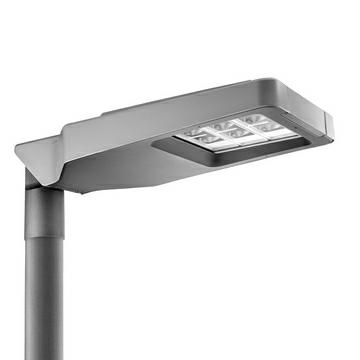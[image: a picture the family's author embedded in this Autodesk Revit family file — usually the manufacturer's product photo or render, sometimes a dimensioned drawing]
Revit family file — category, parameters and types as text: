
# Revit family: Lighting-StreetLighting-GEWISS-ROAD[5]MINI-LED_OPTIC_HUGE_CLI
name_source: partatom
category: Apparecchi per illuminazione
units: mm (PartAtom-declared; Revit-internal decimal feet)

## family parameters
Basato su piano di lavoro = No
Condiviso = No
Punto di calcolo locali = No
Quota connettore circolare = Usa diametro
Sempre verticale = Sì
Sorgente d'illuminazione = No
Taglio con vuoti quando caricato = No
Tipo di parte = Normale

## types (26) — shared parameters
Applicazione = External
Carico apparente = 53 VA
Catalogue = LIGHTING
Catalogue Range = ROAD [5]
Commenti sul wattaggio = 53W
Electrocod = 244C
IDF = 0fc73019-b15a-4bb7-a903-3c2ad933a49c
IDT = 6eb1c969380f487eb4332d009c9c34aa
IP degree = IP66
Immagine tipo = GWR5276M.jpg
Insulation class = I
Lamp- = LED
Lampada = LED
Minimum distance from the illuminated object = 1M
Produttore = GEWISS S.p.A.
SEO = Street lighting
Shock resistance = IK08
Technical sheet = https://www.gewiss.com
Tilt adjustable = -20° ÷ +10° side bracket - -10° ÷ +20° pole head
Tipo alimentatore = Constant Current Driver Led
URL = https://www.gewiss.com
Version file RFA = 20.11
Warranty = 5 years

## per-type parameters (varying)
- GWR5611M - ROAD5 MINI HUGE 1M 4000K 1,0A CL1 1-10V: Colour temperature=4000 K (CRI 70); Colour temperature:=4000 K (CRI 70); Descrizione=ROAD5 MINI HUGE 1M 4000K 1,0A CL1 1-10V; EAN code=8011564874053; LED LifeTime (L80B05)=120000H; LED current.=1A; Lumen output (lm)=3370; Maximum surface exposed to the wind=0,15M2; Modello=GWR5611M; No. Chorus modules=1 (1x3 LED); Nominal flux (lm)=4770; Number of modules=1 (1x3 LED); Operating temperature:=-25 +40 °C; Optic=H - ULOR: 0%; Overvoltage resistance=12 KV (Common and dfferential mode); Pilot current=1A; Power supply operation=Dimmable; System power=38W; Tipologia=Dimmable; Voltage-=220/240 V - 50/60 Hz - Dimmable 1-10 V; Weight (kg)=6,4; Weight (kg):=6,4; Working temperature=-25 +40 °C
- GWR5612B30K - ROAD5 MINI HUGE 2M 3000K 1,0A CL1 BIREG: Body=Die-cast aluminium -; Classification:=-; Color Rendering Index=CRI-70; Colore=Graphite grey; Colour :=Powder coating; Colour temperature=3000K; Colour temperature:=3000 K (CRI>80); Context=Street and parking lighting; Control System=Bi-power with self-learning; DIN 18032-3 certification=-; Descrizione=GWR5612B30K - ROAD5 MINI HUGE 2M 3000K 1,0A CL1 BIREG; Device with reduced surface temperature=-; Driver=Included; Driver Box=Built-in; Efficiency (lm/W)=91; Eletrical and lighting features=-; External screw=Stainless steel; Fixing=Pole Head - Outreach; Gasket=Anti-aging silicone; General information=-; Glow Wire Test :=-; IPEA=ROAD = A + // LARGE AREAS = A + // CYCLOPEDONALS = A // GREEN AREAS = A // HISTORICAL CENTER = A4 +; Installationa and maintenance=-; LED Life Time (L80B05)=120000H; LED Maintenance=Not available; LED current.=1A; Lifetime=L90B10 (Tq+25°C) = 100.000 h - L90B10 (Tq+40°C) = 75.000 h; Locking Hook=Integrated front handle; Lumen output (lm)=7000; Luminaire=LED Road Equipment; Materials=-; Maximum surface exposed to the wind=0,149999999999999M2; Maximum surface exposed to the wind :=0.15 m²; Modello=GWR5612B30K; Mouting and installation=Pole Head - Outreach; Nominal flux (lm)=8280; Number of modules=2 (2x3 LED); Operating temperature :=-25 +40 °C; Operating temperature:=-25 +40 °C; Optic=HUGE; Optic :=Metallized polycarbonate reflector; Optic Maintenance=Not available; Optic and illuminating features=-; Overvoltage protection=DM 10KV / CM 10KV; Overvoltage resistance :=Common and dfferential mode: 10KV; Photobiological Risk Class=RG0; Power supply operation=Bi power; Rated frequency (Hz)=50 / 60; Shield type=4mm thick flat tempered glass; Standard Deviation Colour Matching=SDCM = 5; Standard-=EN 60598-2-3, EN 60598-1 IEC/TR 62778; Standards and approvals=-; Stocking temperature=-; Supply voltage=220 - 240 V; System power=77W; System power :=77 W @ 1A; Tilt-=-20° ÷ +10° side bracket - -10° ÷ +20° pole head; Tipologia=Bi power; Type of light source=LED - Not replaceable; Unified Glare Rating=G*3 - ULOR = 0; Unique digital code (Datamatrix)=Currently not present; Voltage-=220/240 V - 50/60 Hz - Bi-power with self-learning; Weight (kg):=6,6; Wiring=Isolating switch
- GWR561130K - ROAD5 MINI HUGE 1M 3000K 1,0A CL1: Body=Die-cast aluminium -; Classification:=-; Color Rendering Index=CRI-70; Colore=Graphite grey; Colour :=Powder coating; Colour temperature=3000K; Colour temperature:=3000 K (CRI>80); Context=Street and parking lighting; Control System=Stand alone; DIN 18032-3 certification=-; Descrizione=GWR561130K - ROAD5 MINI HUGE 1M 3000K 1,0A CL1; Device with reduced surface temperature=-; Driver=Included; Driver Box=Built-in; Efficiency (lm/W)=92; Eletrical and lighting features=-; External screw=Stainless steel; Fixing=Pole Head - Outreach; Gasket=Anti-aging silicone; General information=-; Glow Wire Test :=-; IPEA=ROAD = A + // LARGE AREAS = A ++ // CYCLOPEDONALS = A + // GREEN AREAS = A + // HISTORICAL CENTER = A4 +; Installationa and maintenance=-; LED Life Time (L80B05)=120000H; LED Maintenance=Not available; LED current.=1A; Lifetime=L90B10 (Tq+25°C) = 100.000 h - L90B10 (Tq+40°C) = 75.000 h; Locking Hook=Integrated front handle; Lumen output (lm)=3500; Luminaire=LED Road Equipment; Materials=-; Maximum surface exposed to the wind=0,149999999999999M2; Maximum surface exposed to the wind :=0.15 m²; Modello=GWR561130K; Mouting and installation=Pole Head - Outreach; Nominal flux (lm)=4140; Number of modules=1 (1x3 LED); Operating temperature :=-25 +40 °C; Operating temperature:=-25 +40 °C; Optic=HUGE; Optic :=Metallized polycarbonate reflector; Optic Maintenance=Not available; Optic and illuminating features=-; Overvoltage protection=DM 10KV / CM 10KV; Overvoltage resistance :=Common and dfferential mode: 10KV; Photobiological Risk Class=RG0; Rated frequency (Hz)=50 / 60; Shield type=4mm thick flat tempered glass; Standard Deviation Colour Matching=SDCM = 5; Standard-=EN 60598-2-3, EN 60598-1 IEC/TR 62778; Standards and approvals=-; Stocking temperature=-; Supply voltage=220 - 240 V; System power=38W; System power :=38 W @ 1A; Tilt-=-20° ÷ +10° side bracket - -10° ÷ +20° pole head; Tipologia=Stand alone; Type of light source=LED - Not replaceable; Unified Glare Rating=G*3 - ULOR = 0; Unique digital code (Datamatrix)=Currently not present; Voltage-=220/240 V - 50/60 Hz - Stand alone; Weight (kg):=6,4; Wiring=Isolating switch
- GWR5672M - ROAD5 MINI HUGE 2M 4000K 0,7A CL1 1-10V: Colour temperature=4000 K (CRI 70); Colour temperature:=4000 K (CRI 70); Descrizione=ROAD5 MINI HUGE 2M 4000K 0,7A CL1 1-10V; EAN code=8011564874473; LED LifeTime (L80B05)=77000H; LED current.=0,7A; Lumen output (lm)=4590; Maximum surface exposed to the wind=0,15M2; Modello=GWR5672M; No. Chorus modules=2 (2x3 LED); Nominal flux (lm)=6240; Number of modules=2 (2x3 LED); Operating temperature:=-25 +50 °C; Optic=H - ULOR: 0%; Overvoltage resistance=12 KV (Common and dfferential mode); Pilot current=0,7A; Power supply operation=Dimmable; System power=53W; Tipologia=Dimmable; Voltage-=220/240 V - 50/60 Hz - Dimmable 1-10 V; Weight (kg)=6,6; Weight (kg):=6,6; Working temperature=-25 +50 °C
- GWR5611B30K - ROAD5 MINI HUGE 1M 3000K 1,0A CL1 BIREG: Body=Die-cast aluminium -; Classification:=-; Color Rendering Index=CRI-70; Colore=Graphite grey; Colour :=Powder coating; Colour temperature=3000K; Colour temperature:=3000 K (CRI>80); Context=Street and parking lighting; Control System=Bi-power with self-learning; DIN 18032-3 certification=-; Descrizione=GWR5611B30K - ROAD5 MINI HUGE 1M 3000K 1,0A CL1 BIREG; Device with reduced surface temperature=-; Driver=Included; Driver Box=Built-in; Efficiency (lm/W)=90; Eletrical and lighting features=-; External screw=Stainless steel; Fixing=Pole Head - Outreach; Gasket=Anti-aging silicone; General information=-; Glow Wire Test :=-; IPEA=ROAD = A + // LARGE AREAS = A + // CYCLOPEDONALS = A // GREEN AREAS = A // HISTORICAL CENTER = A3 +; Installationa and maintenance=-; LED Life Time (L80B05)=120000H; LED Maintenance=Not available; LED current.=1A; Lifetime=L90B10 (Tq+25°C) = 100.000 h - L90B10 (Tq+40°C) = 75.000 h; Locking Hook=Integrated front handle; Lumen output (lm)=3500; Luminaire=LED Road Equipment; Materials=-; Maximum surface exposed to the wind=0,149999999999999M2; Maximum surface exposed to the wind :=0.15 m²; Modello=GWR5611B30K; Mouting and installation=Pole Head - Outreach; Nominal flux (lm)=4140; Number of modules=1 (1x3 LED); Operating temperature :=-25 +40 °C; Operating temperature:=-25 +40 °C; Optic=HUGE; Optic :=Metallized polycarbonate reflector; Optic Maintenance=Not available; Optic and illuminating features=-; Overvoltage protection=DM 10KV / CM 10KV; Overvoltage resistance :=Common and dfferential mode: 10KV; Photobiological Risk Class=RG0; Power supply operation=Bi power; Rated frequency (Hz)=50 / 60; Shield type=4mm thick flat tempered glass; Standard Deviation Colour Matching=SDCM = 5; Standard-=EN 60598-2-3, EN 60598-1 IEC/TR 62778; Standards and approvals=-; Stocking temperature=-; Supply voltage=220 - 240 V; System power=39W; System power :=39 W @ 1A; Tilt-=-20° ÷ +10° side bracket - -10° ÷ +20° pole head; Tipologia=Bi power; Type of light source=LED - Not replaceable; Unified Glare Rating=G*3 - ULOR = 0; Unique digital code (Datamatrix)=Currently not present; Voltage-=220/240 V - 50/60 Hz - Bi-power with self-learning; Weight (kg):=6,4; Wiring=Isolating switch
- GWR5612M - ROAD5 MINI HUGE 2M 4000K 1,0A CL1 1-10V: Colour temperature=4000 K (CRI 70); Colour temperature:=4000 K (CRI 70); Descrizione=ROAD5 MINI HUGE 2M 4000K 1,0A CL1 1-10V; EAN code=8011564874084; LED LifeTime (L80B05)=120000H; LED current.=1A; Lumen output (lm)=6730; Maximum surface exposed to the wind=0,15M2; Modello=GWR5612M; No. Chorus modules=2 (2x3 LED); Nominal flux (lm)=9540; Number of modules=2 (2x3 LED); Operating temperature:=-25 +40 °C; Optic=H - ULOR: 0%; Overvoltage resistance=12 KV (Common and dfferential mode); Pilot current=1A; Power supply operation=Dimmable; System power=76W; Tipologia=Dimmable; Voltage-=220/240 V - 50/60 Hz - Dimmable 1-10 V; Weight (kg)=6,6; Weight (kg):=6,6; Working temperature=-25 +40 °C
- GWR5671M - ROAD5 MINI HUGE 1M 4000K 0,7A CL1 1-10V: Colour temperature=4000 K (CRI 70); Colour temperature:=4000 K (CRI 70); Descrizione=ROAD5 MINI HUGE 1M 4000K 0,7A CL1 1-10V; EAN code=8011564874442; LED LifeTime (L80B05)=77000H; LED current.=0,7A; Lumen output (lm)=2300; Maximum surface exposed to the wind=0,15M2; Modello=GWR5671M; No. Chorus modules=1 (1x3 LED); Nominal flux (lm)=3120; Number of modules=1 (1x3 LED); Operating temperature:=-25 +50 °C; Optic=H - ULOR: 0%; Overvoltage resistance=12 KV (Common and dfferential mode); Pilot current=0,7A; Power supply operation=Dimmable; System power=27W; Tipologia=Dimmable; Voltage-=220/240 V - 50/60 Hz - Dimmable 1-10 V; Weight (kg)=6,4; Weight (kg):=6,4; Working temperature=-25 +50 °C
- GWR5612 - ROAD5 MINI HUGE 2M 4000K 1,0A CL1: Colour temperature=4000 K (CRI 70); Colour temperature:=4000 K (CRI 70); Descrizione=ROAD5 MINI HUGE 2M 4000K 1,0A CL1; EAN code=8011564874060; LED LifeTime (L80B05)=120000H; LED current.=1A; Lumen output (lm)=6730; Maximum surface exposed to the wind=0,15M2; Modello=GWR5612; No. Chorus modules=2 (2x3 LED); Nominal flux (lm)=9540; Number of modules=2 (2x3 LED); Operating temperature:=-25 +40 °C; Optic=H - ULOR: 0%; Overvoltage resistance=12 KV (Common and dfferential mode); Pilot current=1A; System power=76W; Tipologia=Stand alone; Voltage-=220/240 V - 50/60 Hz - Stand alone; Weight (kg)=6,6; Weight (kg):=6,6; Working temperature=-25 +40 °C
- GWR5612B - ROAD5 MINI HUGE 2M 4000K 1,0A CL1 BIREG: Colour temperature=4000 K (CRI 70); Colour temperature:=4000 K (CRI 70); Descrizione=ROAD5 MINI HUGE 2M 4000K 1,0A CL1 BI-POW; EAN code=8011564874077; LED LifeTime (L80B05)=120000H; LED current.=1A; Lumen output (lm)=6730; Maximum surface exposed to the wind=0,15M2; Modello=GWR5612B; No. Chorus modules=2 (2x3 LED); Nominal flux (lm)=9540; Number of modules=2 (2x3 LED); Operating temperature:=-25 +40 °C; Optic=H - ULOR: 0%; Overvoltage resistance=12 KV (Common and dfferential mode); Pilot current=1A; Power supply operation=Bi power; System power=77W; Tipologia=Bi power; Voltage-=220/240 V - 50/60 Hz - Bi-power with self-learning; Weight (kg)=6,6; Weight (kg):=6,6; Working temperature=-25 +40 °C
- GWR5671 - ROAD5 MINI HUGE 1M 4000K 0,7A CL1: Colour temperature=4000 K (CRI 70); Colour temperature:=4000 K (CRI 70); Descrizione=ROAD5 MINI HUGE 1M 4000K 0,7A CL1; EAN code=8011564874428; LED LifeTime (L80B05)=77000H; LED current.=0,7A; Lumen output (lm)=2300; Maximum surface exposed to the wind=0,15M2; Modello=GWR5671; No. Chorus modules=1 (1x3 LED); Nominal flux (lm)=3120; Number of modules=1 (1x3 LED); Operating temperature:=-25 +50 °C; Optic=H - ULOR: 0%; Overvoltage resistance=12 KV (Common and dfferential mode); Pilot current=0,7A; System power=27W; Tipologia=Stand alone; Voltage-=220/240 V - 50/60 Hz - Stand alone; Weight (kg)=6,4; Weight (kg):=6,4; Working temperature=-25 +50 °C
- GWR5611M30K - ROAD5 MINI HUGE 1M 3000K 1,0A CL1 1-10V: Body=Die-cast aluminium -; Classification:=-; Color Rendering Index=CRI-70; Colore=Graphite grey; Colour :=Powder coating; Colour temperature=3000K; Colour temperature:=3000 K (CRI>80); Context=Street and parking lighting; Control System=Dimmable 1-10 V; DIN 18032-3 certification=-; Descrizione=GWR5611M30K - ROAD5 MINI HUGE 1M 3000K 1,0A CL1 1-10V; Device with reduced surface temperature=-; Driver=Included; Driver Box=Built-in; Efficiency (lm/W)=90; Eletrical and lighting features=-; External screw=Stainless steel; Fixing=Pole Head - Outreach; Gasket=Anti-aging silicone; General information=-; Glow Wire Test :=-; IPEA=ROAD = A + // LARGE AREAS = A + // CYCLOPEDONALS = A // GREEN AREAS = A // HISTORICAL CENTER = A3 +; Installationa and maintenance=-; LED Life Time (L80B05)=120000H; LED Maintenance=Not available; LED current.=1A; Lifetime=L90B10 (Tq+25°C) = 100.000 h - L90B10 (Tq+40°C) = 75.000 h; Locking Hook=Integrated front handle; Lumen output (lm)=3500; Luminaire=LED Road Equipment; Materials=-; Maximum surface exposed to the wind=0,149999999999999M2; Maximum surface exposed to the wind :=0.15 m²; Modello=GWR5611M30K; Mouting and installation=Pole Head - Outreach; Nominal flux (lm)=4140; Number of modules=1 (1x3 LED); Operating temperature :=-25 +40 °C; Operating temperature:=-25 +40 °C; Optic=HUGE; Optic :=Metallized polycarbonate reflector; Optic Maintenance=Not available; Optic and illuminating features=-; Overvoltage protection=DM 10KV / CM 10KV; Overvoltage resistance :=Common and dfferential mode: 10KV; Photobiological Risk Class=RG0; Power supply operation=Dimmable; Rated frequency (Hz)=50 / 60; Shield type=4mm thick flat tempered glass; Standard Deviation Colour Matching=SDCM = 5; Standard-=EN 60598-2-3, EN 60598-1 IEC/TR 62778; Standards and approvals=-; Stocking temperature=-; Supply voltage=220 - 240 V; System power=38W; System power :=39 W @ 1A; Tilt-=-20° ÷ +10° side bracket - -10° ÷ +20° pole head; Tipologia=Dimmable; Type of light source=LED - Not replaceable; Unified Glare Rating=G*3 - ULOR = 0; Unique digital code (Datamatrix)=Currently not present; Voltage-=220/240 V - 50/60 Hz - Dimmable 1-10 V; Weight (kg):=6,4; Wiring=Isolating switch
- GWR5672M30K - ROAD5 MINI HUGE 2M 3000K 0,7A CL1 1-10V: Body=Die-cast aluminium -; Classification:=-; Color Rendering Index=CRI-70; Colore=Graphite grey; Colour :=Powder coating; Colour temperature=3000K; Colour temperature:=3000 K (CRI>80); Context=Street and parking lighting; Control System=Dimmable 1-10 V; DIN 18032-3 certification=-; Descrizione=GWR5672M30K - ROAD5 MINI HUGE 2M 3000K 0,7A CL1 1-10V; Device with reduced surface temperature=-; Driver=Included; Driver Box=Built-in; Efficiency (lm/W)=96; Eletrical and lighting features=-; External screw=Stainless steel; Fixing=Pole Head - Outreach; Gasket=Anti-aging silicone; General information=-; Glow Wire Test :=-; IPEA=ROAD = A ++ // LARGE AREAS = A ++ // CYCLOPEDONALS = A + // GREEN AREAS = A + // HISTORICAL CENTER = A5 +; Installationa and maintenance=-; LED Life Time (L80B05)=77000H; LED Maintenance=Not available; LED current.=0,7A; Lifetime=L90B10 (Tq+25°C) = 100.000 h - L90B10 (Tq+50°C) = 75.000 h; Locking Hook=Integrated front handle; Lumen output (lm)=5200; Luminaire=LED Road Equipment; Materials=-; Maximum surface exposed to the wind=0,149999999999999M2; Maximum surface exposed to the wind :=0.15 m²; Modello=GWR5672M30K; Mouting and installation=Pole Head - Outreach; Nominal flux (lm)=5400; Number of modules=2 (2x3 LED); Operating temperature :=-25 +50 °C; Operating temperature:=-25 +50 °C; Optic=HUGE; Optic :=Metallized polycarbonate reflector; Optic Maintenance=Not available; Optic and illuminating features=-; Overvoltage protection=DM 10KV / CM 10KV; Overvoltage resistance :=Common and dfferential mode: 10KV; Photobiological Risk Class=RG0; Power supply operation=Dimmable; Rated frequency (Hz)=50 / 60; Shield type=4mm thick flat tempered glass; Standard Deviation Colour Matching=SDCM = 5; Standard-=EN 60598-2-3, EN 60598-1 IEC/TR 62778; Standards and approvals=-; Stocking temperature=-; Supply voltage=220 - 240 V; System power=53W; System power :=54 W @ 0.7A; Tilt-=-20° ÷ +10° side bracket - -10° ÷ +20° pole head; Tipologia=Dimmable; Type of light source=LED - Not replaceable; Unified Glare Rating=G*3 - ULOR = 0; Unique digital code (Datamatrix)=Currently not present; Voltage-=220/240 V - 50/60 Hz - Dimmable 1-10 V; Weight (kg):=6,6; Wiring=Isolating switch
- GWR561230K - ROAD5 MINI HUGE 2M 3000K 1,0A CL1: Body=Die-cast aluminium -; Classification:=-; Color Rendering Index=CRI-70; Colore=Graphite grey; Colour :=Powder coating; Colour temperature=3000K; Colour temperature:=3000 K (CRI>80); Context=Street and parking lighting; Control System=Stand alone; DIN 18032-3 certification=-; Descrizione=GWR561230K - ROAD5 MINI HUGE 2M 3000K 1,0A CL1; Device with reduced surface temperature=-; Driver=Included; Driver Box=Built-in; Efficiency (lm/W)=97; Eletrical and lighting features=-; External screw=Stainless steel; Fixing=Pole Head - Outreach; Gasket=Anti-aging silicone; General information=-; Glow Wire Test :=-; IPEA=ROAD = A + // LARGE AREAS = A ++ // CYCLOPEDONALS = A + // GREEN AREAS = A + // HISTORICAL CENTER = A5 +; Installationa and maintenance=-; LED Life Time (L80B05)=120000H; LED Maintenance=Not available; LED current.=0,9A; Lifetime=L90B10 (Tq+25°C) = 100.000 h - L90B10 (Tq+40°C) = 75.000 h; Locking Hook=Integrated front handle; Lumen output (lm)=6500; Luminaire=LED Road Equipment; Materials=-; Maximum surface exposed to the wind=0,149999999999999M2; Maximum surface exposed to the wind :=0.15 m²; Modello=GWR561230K; Mouting and installation=Pole Head - Outreach; Nominal flux (lm)=8280; Number of modules=2 (2x3 LED); Operating temperature :=-25 +40 °C; Operating temperature:=-25 +40 °C; Optic=HUGE; Optic :=Metallized polycarbonate reflector; Optic Maintenance=Not available; Optic and illuminating features=-; Overvoltage protection=DM 10KV / CM 10KV; Overvoltage resistance :=Common and dfferential mode: 10KV; Photobiological Risk Class=RG0; Rated frequency (Hz)=50 / 60; Shield type=4mm thick flat tempered glass; Standard Deviation Colour Matching=SDCM = 5; Standard-=EN 60598-2-3, EN 60598-1 IEC/TR 62778; Standards and approvals=-; Stocking temperature=-; Supply voltage=220 - 240 V; System power=76W; System power :=67 W @ 0.9A; Tilt-=-20° ÷ +10° side bracket - -10° ÷ +20° pole head; Tipologia=Stand alone; Type of light source=LED - Not replaceable; Unified Glare Rating=G*3 - ULOR = 0; Unique digital code (Datamatrix)=Currently not present; Voltage-=220/240 V - 50/60 Hz - Stand alone; Weight (kg):=6,6; Wiring=Isolating switch
- GWR5631 - ROAD5 MINI HUGE 1M 4000K 0,35A CL1: Colour temperature=4000 K (CRI 70); Colour temperature:=4000 K (CRI 70); Descrizione=ROAD5 MINI HUGE 1M 4000K 0,35A CL1; EAN code=8011564874411; LED LifeTime (L80B05)=77000H; LED current.=0,35A; Lumen output (lm)=1150; Maximum surface exposed to the wind=0,15M2; Modello=GWR5631; No. Chorus modules=1 (1x3 LED); Nominal flux (lm)=1560; Number of modules=1 (1x3 LED); Operating temperature:=-25 +50 °C; Optic=H - ULOR: 0%; Overvoltage resistance=12 KV (Common and dfferential mode); Pilot current=0,35A; System power=14W; Tipologia=Stand alone; Voltage-=220/240 V - 50/60 Hz - Stand alone; Weight (kg)=6,4; Weight (kg):=6,4; Working temperature=-25 +50 °C
- GWR5671B - ROAD5 MINI HUGE 1M 4000K 0,7A CL1 BIREG: Colour temperature=4000 K (CRI 70); Colour temperature:=4000 K (CRI 70); Descrizione=ROAD5 MINI HUGE 1M 4000K 0,7A CL1 BI-POW; EAN code=8011564874435; LED LifeTime (L80B05)=77000H; LED current.=0,7A; Lumen output (lm)=2300; Maximum surface exposed to the wind=0,15M2; Modello=GWR5671B; No. Chorus modules=1 (1x3 LED); Nominal flux (lm)=3120; Number of modules=1 (1x3 LED); Operating temperature:=-25 +50 °C; Optic=H - ULOR: 0%; Overvoltage resistance=12 KV (Common and dfferential mode); Pilot current=0,7A; Power supply operation=Bi power; System power=28W; Tipologia=Bi power; Voltage-=220/240 V - 50/60 Hz - Bi-power with self-learning; Weight (kg)=6,4; Weight (kg):=6,4; Working temperature=-25 +50 °C
- GWR5611B - ROAD5 MINI HUGE 1M 4000K 1,0A CL1 BIREG: Colour temperature=4000 K (CRI 70); Colour temperature:=4000 K (CRI 70); Descrizione=ROAD5 MINI HUGE 1M 4000K 1,0A CL1 BI-POW; EAN code=8011564874046; LED LifeTime (L80B05)=120000H; LED current.=1A; Lumen output (lm)=3370; Maximum surface exposed to the wind=0,15M2; Modello=GWR5611B; No. Chorus modules=1 (1x3 LED); Nominal flux (lm)=4770; Number of modules=1 (1x3 LED); Operating temperature:=-25 +40 °C; Optic=H - ULOR: 0%; Overvoltage resistance=12 KV (Common and dfferential mode); Pilot current=1A; Power supply operation=Bi power; System power=39W; Tipologia=Bi power; Voltage-=220/240 V - 50/60 Hz - Bi-power with self-learning; Weight (kg)=6,4; Weight (kg):=6,4; Working temperature=-25 +40 °C
- GWR5612M30K - ROAD5 MINI HUGE 2M 3000K 1,0A CL1 1-10V: Body=Die-cast aluminium -; Classification:=-; Color Rendering Index=CRI-70; Colore=Graphite grey; Colour :=Powder coating; Colour temperature=3000K; Colour temperature:=3000 K (CRI>80); Context=Street and parking lighting; Control System=Dimmable 1-10 V; DIN 18032-3 certification=-; Descrizione=GWR5612M30K - ROAD5 MINI HUGE 2M 3000K 1,0A CL1 1-10V; Device with reduced surface temperature=-; Driver=Included; Driver Box=Built-in; Efficiency (lm/W)=91; Eletrical and lighting features=-; External screw=Stainless steel; Fixing=Pole Head - Outreach; Gasket=Anti-aging silicone; General information=-; Glow Wire Test :=-; IPEA=ROAD = A + // LARGE AREAS = A + // CYCLOPEDONALS = A // GREEN AREAS = A // HISTORICAL CENTER = A4 +; Installationa and maintenance=-; LED Life Time (L80B05)=120000H; LED Maintenance=Not available; LED current.=1A; Lifetime=L90B10 (Tq+25°C) = 100.000 h - L90B10 (Tq+40°C) = 75.000 h; Locking Hook=Integrated front handle; Lumen output (lm)=7000; Luminaire=LED Road Equipment; Materials=-; Maximum surface exposed to the wind=0,149999999999999M2; Maximum surface exposed to the wind :=0.15 m²; Modello=GWR5612M30K; Mouting and installation=Pole Head - Outreach; Nominal flux (lm)=8280; Number of modules=2 (2x3 LED); Operating temperature :=-25 +40 °C; Operating temperature:=-25 +40 °C; Optic=HUGE; Optic :=Metallized polycarbonate reflector; Optic Maintenance=Not available; Optic and illuminating features=-; Overvoltage protection=DM 10KV / CM 10KV; Overvoltage resistance :=Common and dfferential mode: 10KV; Photobiological Risk Class=RG0; Power supply operation=Dimmable; Rated frequency (Hz)=50 / 60; Shield type=4mm thick flat tempered glass; Standard Deviation Colour Matching=SDCM = 5; Standard-=EN 60598-2-3, EN 60598-1 IEC/TR 62778; Standards and approvals=-; Stocking temperature=-; Supply voltage=220 - 240 V; System power=76W; System power :=77 W @ 1A; Tilt-=-20° ÷ +10° side bracket - -10° ÷ +20° pole head; Tipologia=Dimmable; Type of light source=LED - Not replaceable; Unified Glare Rating=G*3 - ULOR = 0; Unique digital code (Datamatrix)=Currently not present; Voltage-=220/240 V - 50/60 Hz - Dimmable 1-10 V; Weight (kg):=6,6; Wiring=Isolating switch
- GWR5671B30K - ROAD5 MINI HUGE 1M 3000K 0,7A CL1 BIREG: Body=Die-cast aluminium -; Classification:=-; Color Rendering Index=CRI-70; Colore=Graphite grey; Colour :=Powder coating; Colour temperature=3000K; Colour temperature:=3000 K (CRI>80); Context=Street and parking lighting; Control System=Bi-power with self-learning; DIN 18032-3 certification=-; Descrizione=GWR5671B30K - ROAD5 MINI HUGE 1M 3000K 0,7A CL1 BIREG; Device with reduced surface temperature=-; Driver=Included; Driver Box=Built-in; Efficiency (lm/W)=93; Eletrical and lighting features=-; External screw=Stainless steel; Fixing=Pole Head - Outreach; Gasket=Anti-aging silicone; General information=-; Glow Wire Test :=-; IPEA=ROAD = A + // LARGE AREAS = A ++ // CYCLOPEDONALS = A + // GREEN AREAS = A + // HISTORICAL CENTER = A4 +; Installationa and maintenance=-; LED Life Time (L80B05)=77000H; LED Maintenance=Not available; LED current.=0,7A; Lifetime=L90B10 (Tq+25°C) = 100.000 h - L90B10 (Tq+50°C) = 75.000 h; Locking Hook=Integrated front handle; Lumen output (lm)=2600; Luminaire=LED Road Equipment; Materials=-; Maximum surface exposed to the wind=0,149999999999999M2; Maximum surface exposed to the wind :=0.15 m²; Modello=GWR5671B30K; Mouting and installation=Pole Head - Outreach; Nominal flux (lm)=2700; Number of modules=1 (1x3 LED); Operating temperature :=-25 +50 °C; Operating temperature:=-25 +50 °C; Optic=HUGE; Optic :=Metallized polycarbonate reflector; Optic Maintenance=Not available; Optic and illuminating features=-; Overvoltage protection=DM 10KV / CM 10KV; Overvoltage resistance :=Common and dfferential mode: 10KV; Photobiological Risk Class=RG0; Power supply operation=Bi power; Rated frequency (Hz)=50 / 60; Shield type=4mm thick flat tempered glass; Standard Deviation Colour Matching=SDCM = 5; Standard-=EN 60598-2-3, EN 60598-1 IEC/TR 62778; Standards and approvals=-; Stocking temperature=-; Supply voltage=220 - 240 V; System power=28W; System power :=28 W @ 0.7A; Tilt-=-20° ÷ +10° side bracket - -10° ÷ +20° pole head; Tipologia=Bi power; Type of light source=LED - Not replaceable; Unified Glare Rating=G*3 - ULOR = 0; Unique digital code (Datamatrix)=Currently not present; Voltage-=220/240 V - 50/60 Hz - Bi-power with self-learning; Weight (kg):=6,4; Wiring=Isolating switch
- GWR5611 - ROAD5 MINI HUGE 1M 4000K 1,0A CL1: Colour temperature=4000 K (CRI 70); Colour temperature:=4000 K (CRI 70); Descrizione=ROAD5 MINI HUGE 1M 4000K 1,0A CL1; EAN code=8011564874039; LED LifeTime (L80B05)=120000H; LED current.=1A; Lumen output (lm)=3370; Maximum surface exposed to the wind=0,15M2; Modello=GWR5611; No. Chorus modules=1 (1x3 LED); Nominal flux (lm)=4770; Number of modules=1 (1x3 LED); Operating temperature:=-25 +40 °C; Optic=H - ULOR: 0%; Overvoltage resistance=12 KV (Common and dfferential mode); Pilot current=1A; System power=38W; Tipologia=Stand alone; Voltage-=220/240 V - 50/60 Hz - Stand alone; Weight (kg)=6,4; Weight (kg):=6,4; Working temperature=-25 +40 °C
- GWR567130K - ROAD5 MINI HUGE 1M 3000K 0,7A CL1: Body=Die-cast aluminium -; Classification:=-; Color Rendering Index=CRI-70; Colore=Graphite grey; Colour :=Powder coating; Colour temperature=3000K; Colour temperature:=3000 K (CRI>80); Context=Street and parking lighting; Control System=Stand alone; DIN 18032-3 certification=-; Descrizione=GWR567130K - ROAD5 MINI HUGE 1M 3000K 0,7A CL1; Device with reduced surface temperature=-; Driver=Included; Driver Box=Built-in; Efficiency (lm/W)=96; Eletrical and lighting features=-; External screw=Stainless steel; Fixing=Pole Head - Outreach; Gasket=Anti-aging silicone; General information=-; Glow Wire Test :=-; IPEA=ROAD = A ++ // LARGE AREAS = A ++ // CYCLOPEDONALS = A + // GREEN AREAS = A + // HISTORICAL CENTER = A5 +; Installationa and maintenance=-; LED Life Time (L80B05)=77000H; LED Maintenance=Not available; LED current.=0,7A; Lifetime=L90B10 (Tq+25°C) = 100.000 h - L90B10 (Tq+50°C) = 75.000 h; Locking Hook=Integrated front handle; Lumen output (lm)=2600; Luminaire=LED Road Equipment; Materials=-; Maximum surface exposed to the wind=0,149999999999999M2; Maximum surface exposed to the wind :=0.15 m²; Modello=GWR567130K; Mouting and installation=Pole Head - Outreach; Nominal flux (lm)=2700; Number of modules=1 (1x3 LED); Operating temperature :=-25 +50 °C; Operating temperature:=-25 +50 °C; Optic=HUGE; Optic :=Metallized polycarbonate reflector; Optic Maintenance=Not available; Optic and illuminating features=-; Overvoltage protection=DM 10KV / CM 10KV; Overvoltage resistance :=Common and dfferential mode: 10KV; Photobiological Risk Class=RG0; Rated frequency (Hz)=50 / 60; Shield type=4mm thick flat tempered glass; Standard Deviation Colour Matching=SDCM = 5; Standard-=EN 60598-2-3, EN 60598-1 IEC/TR 62778; Standards and approvals=-; Stocking temperature=-; Supply voltage=220 - 240 V; System power=27W; System power :=27 W @ 0.7A; Tilt-=-20° ÷ +10° side bracket - -10° ÷ +20° pole head; Tipologia=Stand alone; Type of light source=LED - Not replaceable; Unified Glare Rating=G*3 - ULOR = 0; Unique digital code (Datamatrix)=Currently not present; Voltage-=220/240 V - 50/60 Hz - Stand alone; Weight (kg):=6,4; Wiring=Isolating switch
- GWR563130K - ROAD5 MINI HUGE 1M 3000K 0,35A CL1: Body=Die-cast aluminium -; Classification:=-; Color Rendering Index=CRI-70; Colore=Graphite grey; Colour :=Powder coating; Colour temperature=3000K; Colour temperature:=3000 K (CRI>80); Context=Street and parking lighting; Control System=Stand alone; DIN 18032-3 certification=-; Descrizione=GWR563130K - ROAD5 MINI HUGE 1M 3000K 0,35A CL1; Device with reduced surface temperature=-; Driver=Included; Driver Box=Built-in; Efficiency (lm/W)=108; Eletrical and lighting features=-; External screw=Stainless steel; Fixing=Pole Head - Outreach; Gasket=Anti-aging silicone; General information=-; Glow Wire Test :=-; IPEA=ROAD = A3 + // LARGE AREAS = A4 + // CYCLOPEDONALS = A3 + // GREEN AREAS = A3 + // HISTORICAL CENTER = A6 +; Installationa and maintenance=-; LED Life Time (L80B05)=77000H; LED Maintenance=Not available; LED current.=0,35A; Lifetime=L90B10 (Tq+25°C) = 100.000 h - L90B10 (Tq+50°C) = 75.000 h; Locking Hook=Integrated front handle; Lumen output (lm)=1400; Luminaire=LED Road Equipment; Materials=-; Maximum surface exposed to the wind=0,149999999999999M2; Maximum surface exposed to the wind :=0.15 m²; Modello=GWR563130K; Mouting and installation=Pole Head - Outreach; Nominal flux (lm)=1350; Number of modules=1 (1x3 LED); Operating temperature :=-25 +50 °C; Operating temperature:=-25 +50 °C; Optic=HUGE; Optic :=Metallized polycarbonate reflector; Optic Maintenance=Not available; Optic and illuminating features=-; Overvoltage protection=DM 10KV / CM 10KV; Overvoltage resistance :=Common and dfferential mode: 10KV; Photobiological Risk Class=RG0; Rated frequency (Hz)=50 / 60; Shield type=4mm thick flat tempered glass; Standard Deviation Colour Matching=SDCM = 5; Standard-=EN 60598-2-3, EN 60598-1 IEC/TR 62778; Standards and approvals=-; Stocking temperature=-; Supply voltage=220 - 240 V; System power=14W; System power :=13 W @ 0.35A; Tilt-=-20° ÷ +10° side bracket - -10° ÷ +20° pole head; Tipologia=Stand alone; Type of light source=LED - Not replaceable; Unified Glare Rating=G*3 - ULOR = 0; Unique digital code (Datamatrix)=Currently not present; Voltage-=220/240 V - 50/60 Hz - Stand alone; Weight (kg):=6,4; Wiring=Isolating switch
- GWR5672B - ROAD5 MINI HUGE 2M 4000K 0,7A CL1 BIREG: Colour temperature=4000 K (CRI 70); Colour temperature:=4000 K (CRI 70); Descrizione=ROAD5 MINI HUGE 2M 4000K 0,7A CL1 BI-POW; EAN code=8011564874466; LED LifeTime (L80B05)=77000H; LED current.=0,7A; Lumen output (lm)=4590; Maximum surface exposed to the wind=0,15M2; Modello=GWR5672B; No. Chorus modules=2 (2x3 LED); Nominal flux (lm)=6240; Number of modules=2 (2x3 LED); Operating temperature:=-25 +50 °C; Optic=H - ULOR: 0%; Overvoltage resistance=12 KV (Common and dfferential mode); Pilot current=0,7A; Power supply operation=Bi power; System power=54W; Tipologia=Bi power; Voltage-=220/240 V - 50/60 Hz - Bi-power with self-learning; Weight (kg)=6,6; Weight (kg):=6,6; Working temperature=-25 +50 °C
- GWR5672B30K - ROAD5 MINI HUGE 2M 3000K 0,7A CL1 BIREG: Body=Die-cast aluminium -; Classification:=-; Color Rendering Index=CRI-70; Colore=Graphite grey; Colour :=Powder coating; Colour temperature=3000K; Colour temperature:=3000 K (CRI>80); Context=Street and parking lighting; Control System=Bi-power with self-learning; DIN 18032-3 certification=-; Descrizione=GWR5672B30K - ROAD5 MINI HUGE 2M 3000K 0,7A CL1 BIREG; Device with reduced surface temperature=-; Driver=Included; Driver Box=Built-in; Efficiency (lm/W)=96; Eletrical and lighting features=-; External screw=Stainless steel; Fixing=Pole Head - Outreach; Gasket=Anti-aging silicone; General information=-; Glow Wire Test :=-; IPEA=ROAD = A ++ // LARGE AREAS = A ++ // CYCLOPEDONALS = A + // GREEN AREAS = A + // HISTORICAL CENTER = A5 +; Installationa and maintenance=-; LED Life Time (L80B05)=77000H; LED Maintenance=Not available; LED current.=0,7A; Lifetime=L90B10 (Tq+25°C) = 100.000 h - L90B10 (Tq+50°C) = 75.000 h; Locking Hook=Integrated front handle; Lumen output (lm)=5200; Luminaire=LED Road Equipment; Materials=-; Maximum surface exposed to the wind=0,149999999999999M2; Maximum surface exposed to the wind :=0.15 m²; Modello=GWR5672B30K; Mouting and installation=Pole Head - Outreach; Nominal flux (lm)=5400; Number of modules=2 (2x3 LED); Operating temperature :=-25 +50 °C; Operating temperature:=-25 +50 °C; Optic=HUGE; Optic :=Metallized polycarbonate reflector; Optic Maintenance=Not available; Optic and illuminating features=-; Overvoltage protection=DM 10KV / CM 10KV; Overvoltage resistance :=Common and dfferential mode: 10KV; Photobiological Risk Class=RG0; Power supply operation=Bi power; Rated frequency (Hz)=50 / 60; Shield type=4mm thick flat tempered glass; Standard Deviation Colour Matching=SDCM = 5; Standard-=EN 60598-2-3, EN 60598-1 IEC/TR 62778; Standards and approvals=-; Stocking temperature=-; Supply voltage=220 - 240 V; System power=54W; System power :=54 W @ 0.7A; Tilt-=-20° ÷ +10° side bracket - -10° ÷ +20° pole head; Tipologia=Bi power; Type of light source=LED - Not replaceable; Unified Glare Rating=G*3 - ULOR = 0; Unique digital code (Datamatrix)=Currently not present; Voltage-=220/240 V - 50/60 Hz - Bi-power with self-learning; Weight (kg):=6,6; Wiring=Isolating switch
- GWR567230K - ROAD5 MINI HUGE 2M 3000K 0,7A CL1: Body=Die-cast aluminium -; Classification:=-; Color Rendering Index=CRI-70; Colore=Graphite grey; Colour :=Powder coating; Colour temperature=3000K; Colour temperature:=3000 K (CRI>80); Context=Street and parking lighting; Control System=Stand alone; DIN 18032-3 certification=-; Descrizione=GWR567230K - ROAD5 MINI HUGE 2M 3000K 0,7A CL1; Device with reduced surface temperature=-; Driver=Included; Driver Box=Built-in; Efficiency (lm/W)=98; Eletrical and lighting features=-; External screw=Stainless steel; Fixing=Pole Head - Outreach; Gasket=Anti-aging silicone; General information=-; Glow Wire Test :=-; IPEA=ROAD = A ++ // LARGE AREAS = A3 + // CYCLOPEDONALS = A ++ // GREEN AREAS = A ++ // HISTORICAL CENTER = A5 +; Installationa and maintenance=-; LED Life Time (L80B05)=77000H; LED Maintenance=Not available; LED current.=0,7A; Lifetime=L90B10 (Tq+25°C) = 100.000 h - L90B10 (Tq+50°C) = 75.000 h; Locking Hook=Integrated front handle; Lumen output (lm)=5200; Luminaire=LED Road Equipment; Materials=-; Maximum surface exposed to the wind=0,149999999999999M2; Maximum surface exposed to the wind :=0.15 m²; Modello=GWR567230K; Mouting and installation=Pole Head - Outreach; Nominal flux (lm)=5400; Number of modules=2 (2x3 LED); Operating temperature :=-25 +50 °C; Operating temperature:=-25 +50 °C; Optic=HUGE; Optic :=Metallized polycarbonate reflector; Optic Maintenance=Not available; Optic and illuminating features=-; Overvoltage protection=DM 10KV / CM 10KV; Overvoltage resistance :=Common and dfferential mode: 10KV; Photobiological Risk Class=RG0; Rated frequency (Hz)=50 / 60; Shield type=4mm thick flat tempered glass; Standard Deviation Colour Matching=SDCM = 5; Standard-=EN 60598-2-3, EN 60598-1 IEC/TR 62778; Standards and approvals=-; Stocking temperature=-; Supply voltage=220 - 240 V; System power=53W; System power :=53 W @ 0.7A; Tilt-=-20° ÷ +10° side bracket - -10° ÷ +20° pole head; Tipologia=Stand alone; Type of light source=LED - Not replaceable; Unified Glare Rating=G*3 - ULOR = 0; Unique digital code (Datamatrix)=Currently not present; Voltage-=220/240 V - 50/60 Hz - Stand alone; Weight (kg):=6,6; Wiring=Isolating switch
- GWR5672 - ROAD5 MINI HUGE 2M 4000K 0,7A CL1: Colour temperature=4000 K (CRI 70); Colour temperature:=4000 K (CRI 70); Descrizione=ROAD5 MINI HUGE 2M 4000K 0,7A CL1; EAN code=8011564874459; LED LifeTime (L80B05)=77000H; LED current.=0,7A; Lumen output (lm)=4590; Maximum surface exposed to the wind=0,15M2; Modello=GWR5672; No. Chorus modules=2 (2x3 LED); Nominal flux (lm)=6240; Number of modules=2 (2x3 LED); Operating temperature:=-25 +50 °C; Optic=H - ULOR: 0%; Overvoltage resistance=12 KV (Common and dfferential mode); Pilot current=0,7A; System power=53W; Tipologia=Stand alone; Voltage-=220/240 V - 50/60 Hz - Stand alone; Weight (kg)=6,6; Weight (kg):=6,6; Working temperature=-25 +50 °C
- GWR5671M30K - ROAD5 MINI HUGE 1M 3000K 0,7A CL1 1-10V: Body=Die-cast aluminium -; Classification:=-; Color Rendering Index=CRI-70; Colore=Graphite grey; Colour :=Powder coating; Colour temperature=3000K; Colour temperature:=3000 K (CRI>80); Context=Street and parking lighting; Control System=Dimmable 1-10 V; DIN 18032-3 certification=-; Descrizione=GWR5671M30K - ROAD5 MINI HUGE 1M 3000K 0,7A CL1 1-10V; Device with reduced surface temperature=-; Driver=Included; Driver Box=Built-in; Efficiency (lm/W)=93; Eletrical and lighting features=-; External screw=Stainless steel; Fixing=Pole Head - Outreach; Gasket=Anti-aging silicone; General information=-; Glow Wire Test :=-; IPEA=ROAD = A + // LARGE AREAS = A ++ // CYCLOPEDONALS = A + // GREEN AREAS = A + // HISTORICAL CENTER = A4 +; Installationa and maintenance=-; LED Life Time (L80B05)=77000H; LED Maintenance=Not available; LED current.=0,7A; Lifetime=L90B10 (Tq+25°C) = 100.000 h - L90B10 (Tq+50°C) = 75.000 h; Locking Hook=Integrated front handle; Lumen output (lm)=2600; Luminaire=LED Road Equipment; Materials=-; Maximum surface exposed to the wind=0,149999999999999M2; Maximum surface exposed to the wind :=0.15 m²; Modello=GWR5671M30K; Mouting and installation=Pole Head - Outreach; Nominal flux (lm)=2700; Number of modules=1 (1x3 LED); Operating temperature :=-25 +50 °C; Operating temperature:=-25 +50 °C; Optic=HUGE; Optic :=Metallized polycarbonate reflector; Optic Maintenance=Not available; Optic and illuminating features=-; Overvoltage protection=DM 10KV / CM 10KV; Overvoltage resistance :=Common and dfferential mode: 10KV; Photobiological Risk Class=RG0; Power supply operation=Dimmable; Rated frequency (Hz)=50 / 60; Shield type=4mm thick flat tempered glass; Standard Deviation Colour Matching=SDCM = 5; Standard-=EN 60598-2-3, EN 60598-1 IEC/TR 62778; Standards and approvals=-; Stocking temperature=-; Supply voltage=220 - 240 V; System power=27W; System power :=28 W @ 0.7A; Tilt-=-20° ÷ +10° side bracket - -10° ÷ +20° pole head; Tipologia=Dimmable; Type of light source=LED - Not replaceable; Unified Glare Rating=G*3 - ULOR = 0; Unique digital code (Datamatrix)=Currently not present; Voltage-=220/240 V - 50/60 Hz - Dimmable 1-10 V; Weight (kg):=6,4; Wiring=Isolating switch
